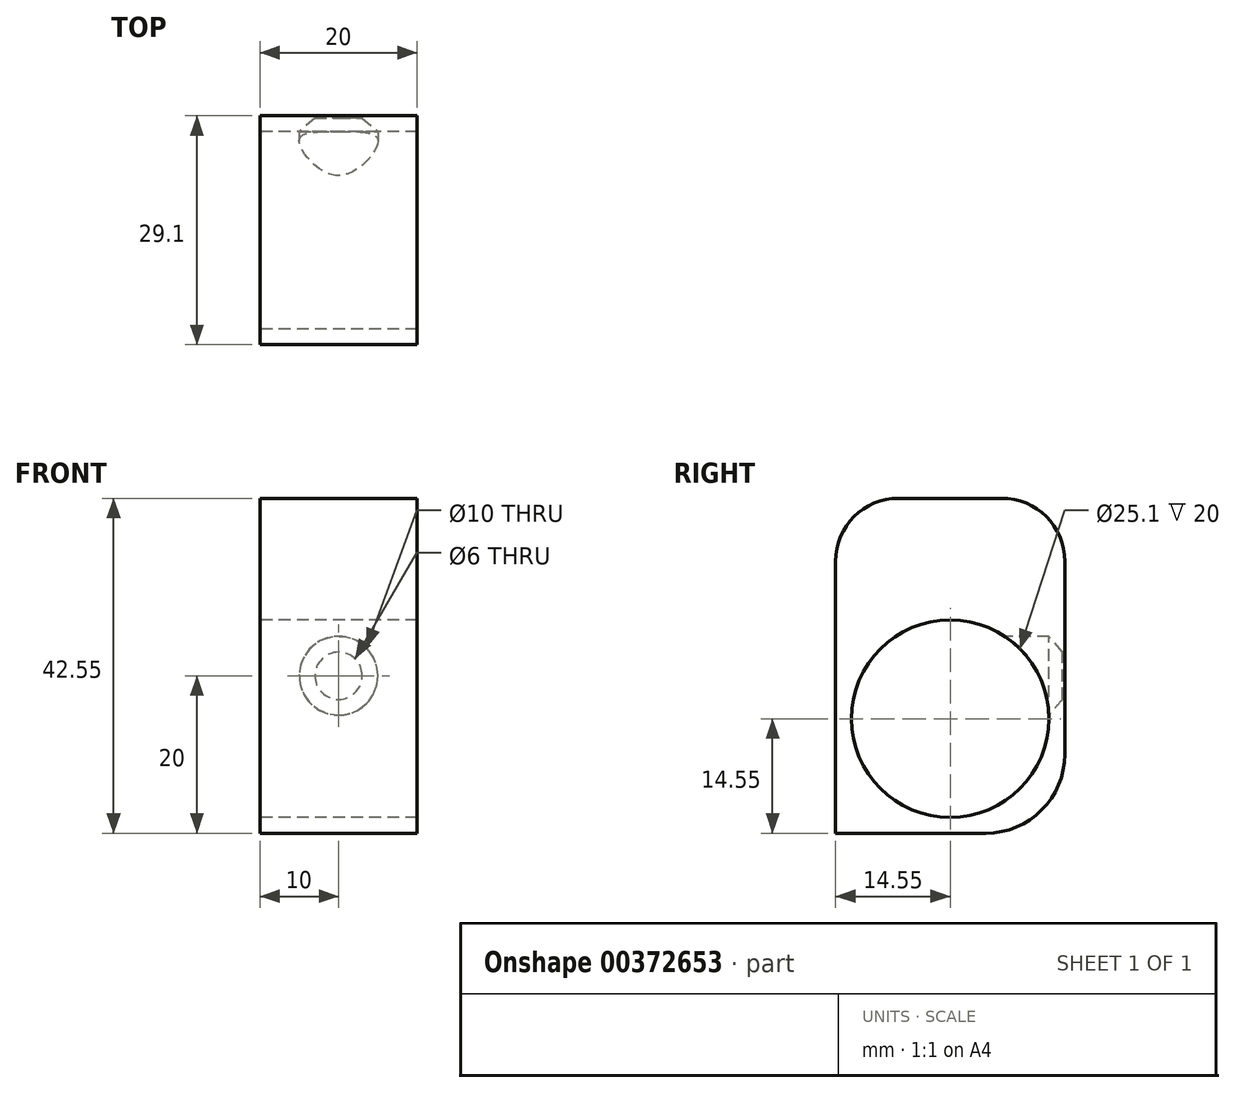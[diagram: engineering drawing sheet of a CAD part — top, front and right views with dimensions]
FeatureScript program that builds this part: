
annotation { "Feature Type Name" : "Feature", "Feature Type Description" : "" }
export const myFeature = defineFeature(function(context is Context, id is Id, definition is map)
    precondition{}
    {
        {
            var Q0;
            Q0=qCreatedBy(makeId("Right.planeOp"),FACE);
            var sketch = newSketch(context, id + "F0", { "sketchPlane" : qUnion([Q0])});
            skCircle(sketch, "E0", {"center": v(0, 0) * mm, "radius": 12.55 * mm});
            skCircle(sketch, "E1", {"center": v(-6.84, 18.8) * mm, "radius": 4.3 * mm, "construction": true});
            skCircle(sketch, "E2", {"center": v(6.84, 18.8) * mm, "radius": 4 * mm});
            skLineSegment(sketch, "E3", {"start": v(-6.84, 18.8) * mm, "end": v(0, 0) * mm, "construction": true});
            skLineSegment(sketch, "E4", {"start": v(6.84, 18.8) * mm, "end": v(0, 0) * mm, "construction": true});
            skCircle(sketch, "E5", {"center": v(-26, 0) * mm, "radius": 11 * mm});
            skLineSegment(sketch, "E6", {"start": v(-26, 0) * mm, "end": v(0, 0) * mm, "construction": true});
            skLineSegment(sketch, "E7", {"start": v(6.55, 28) * mm, "end": v(-6.55, 28) * mm});
            skLineSegment(sketch, "E8", {"start": v(14.55, 20) * mm, "end": v(14.55, -14.55) * mm});
            skLineSegment(sketch, "E9", {"start": v(-14.55, 20) * mm, "end": v(-14.55, -14.55) * mm});
            skLineSegment(sketch, "E10", {"start": v(-14.55, -14.55) * mm, "end": v(14.55, -14.55) * mm});
            skCircle(sketch, "E11", {"center": v(-6.84, 18.8) * mm, "radius": 2.75 * mm});
            skLineSegment(sketch, "E12", {"start": v(0, -14.55) * mm, "end": v(0, 0) * mm, "construction": true});
            skPoint(sketch, "E13.visualSharp", {"position": v(-14.55, 28) * mm});
            skArc(sketch, "E13.filletArc", {"start": v(-6.55, 28) * mm, "mid": v(-12.2, 25.66) * mm, "end": v(-14.55, 20) * mm});
            skPoint(sketch, "E14.visualSharp", {"position": v(14.55, 28) * mm});
            skArc(sketch, "E14.filletArc", {"start": v(14.55, 20) * mm, "mid": v(12.2, 25.66) * mm, "end": v(6.55, 28) * mm});
            skSolve(sketch);
        }
        {
            var Q0;
            Q0=makeQuery(id+"F0.imprint","IMPRINT",FACE,{"disambiguationData":[TD([[makeQuery(id+"F0.imprint","IMPRINT",EDGE,{"derivedFrom":sQuery(id+"F0.wireOp",EDGE,"E0")}),-1.0]])]});
            var Q1;
            Q1=makeQuery(id+"F0.imprint","IMPRINT",FACE,{"disambiguationData":[TD([[makeQuery(id+"F0.imprint","IMPRINT",EDGE,{"derivedFrom":sQuery(id+"F0.wireOp",EDGE,"E2")}),1.0]])]});
            var Q2;
            Q2=makeQuery(id+"F0.imprint","IMPRINT",FACE,{"disambiguationData":[TD([[makeQuery(id+"F0.imprint","IMPRINT",EDGE,{"derivedFrom":sQuery(id+"F0.wireOp",EDGE,"E11")}),1.0]])]});
            extrude(context, id + "F1", {"entities" : qUnion([Q0, Q1, Q2]), "depth" : 20 * mm, "offsetDistance" : 25 * mm, "symmetric" : true});
        }
        {
            var Q0;
            Q0=makeQuery(id+"F1.opExtrude","SWEPT_EDGE",EDGE,{"disambiguationData":[OSD([sQuery(id+"F0.wireOp",EDGE,"XYx4FfuK-tnTQ-wQDn-o0lU-hYzAaBfXhwYU"),sQuery(id+"F0.wireOp",EDGE,"E7")])]});
            var Q1;
            Q1=makeQuery(id+"F1.opExtrude","SWEPT_EDGE",EDGE,{"disambiguationData":[OSD([sQuery(id+"F0.wireOp",EDGE,"ezvYwHDF-qibp-4aTS-obrj-ytzPbMtdMMT9"),sQuery(id+"F0.wireOp",EDGE,"E8")])]});
            var Q2;
            Q2=makeQuery(id+"F1.opExtrude","SWEPT_EDGE",EDGE,{"disambiguationData":[OSD([sQuery(id+"F0.wireOp",EDGE,"ezvYwHDF-qibp-4aTS-obrj-ytzPbMtdMMT9"),sQuery(id+"F0.wireOp",EDGE,"E7")])]});
            var Q3;
            Q3=makeQuery(id+"F1.opExtrude","SWEPT_EDGE",EDGE,{"disambiguationData":[OSD([sQuery(id+"F0.wireOp",EDGE,"E8"),sQuery(id+"F0.wireOp",EDGE,"E10")])]});
            fillet(context, id + "F2", {"entities" : qUnion([Q0, Q1, Q2, Q3]), "radius" : 10 * mm, "tangentPropagation" : true, "allowEdgeOverflow" : false});
        }
        {
            var Q0;
            Q0=qCreatedBy(makeId("Front.planeOp"),FACE);
            var sketch = newSketch(context, id + "F3", { "sketchPlane" : qUnion([Q0])});
            skCircle(sketch, "E15", {"center": v(0, 5.45) * mm, "radius": 2.9 * mm});
            skCircle(sketch, "E16", {"center": v(0, 5.45) * mm, "radius": 5 * mm});
            skSolve(sketch);
        }
        {
            var Q0;
            Q0=makeQuery(id+"F3.imprint","IMPRINT",FACE,{"disambiguationData":[TD([[makeQuery(id+"F3.imprint","IMPRINT",EDGE,{"derivedFrom":sQuery(id+"F3.wireOp",EDGE,"E15")}),1.0]])]});
            extrude(context, id + "F4", {"entities" : qUnion([Q0]), "operationType" : NewBodyOperationType.REMOVE, "endBound" : BoundingType.THROUGH_ALL, "oppositeDirection" : true, "depth" : 25 * mm, "offsetDistance" : 25 * mm});
        }
        {
            var Q0;
            Q0=makeQuery(id+"F3.imprint","IMPRINT",FACE,{"disambiguationData":[TD([[makeQuery(id+"F3.imprint","IMPRINT",EDGE,{"derivedFrom":sQuery(id+"F3.wireOp",EDGE,"E15")}),-1.0]])]});
            extrude(context, id + "F5", {"entities" : qUnion([Q0]), "operationType" : NewBodyOperationType.REMOVE, "flatOperationType" : FlatOperationType.REMOVE, "oppositeDirection" : true, "depth" : 12.5 * mm, "offsetDistance" : 25 * mm, "domain" : OperationDomain.MODEL});
        }
        {
            var Q0;
            Q0=qCreatedBy(makeId("Right.planeOp"),FACE);
            var sketch = newSketch(context, id + "F6", { "sketchPlane" : qUnion([Q0])});
            skLineSegment(sketch, "E17", {"start": v(0, 5.45) * mm, "end": v(14.55, 5.45) * mm, "construction": true});
            skLineSegment(sketch, "E18", {"start": v(14.55, 8.45) * mm, "end": v(14.25, 8.45) * mm});
            skLineSegment(sketch, "E19", {"start": v(14.25, 8.45) * mm, "end": v(12.55, 10.45) * mm});
            skLineSegment(sketch, "E20", {"start": v(11.55, 5.45) * mm, "end": v(14.55, 5.45) * mm});
            skLineSegment(sketch, "E21", {"start": v(14.55, 5.45) * mm, "end": v(14.55, 8.45) * mm});
            skLineSegment(sketch, "E22", {"start": v(12.55, 10.45) * mm, "end": v(11.55, 10.45) * mm});
            skLineSegment(sketch, "E23", {"start": v(11.55, 10.45) * mm, "end": v(11.55, 5.45) * mm});
            skSolve(sketch);
        }
        {
            var Q0;
            Q0=qSketchRegion(id+"F6",true);
            var Q1;
            Q1=sQuery(id+"F6.wireOp",EDGE,"E17");
            revolve(context, id + "F7", {"operationType" : NewBodyOperationType.REMOVE, "surfaceOperationType" : NewSurfaceOperationType.NEW, "entities" : qUnion([Q0]), "axis" : qUnion([Q1]), "revolveType" : RevolveType.FULL});
        }
    });
